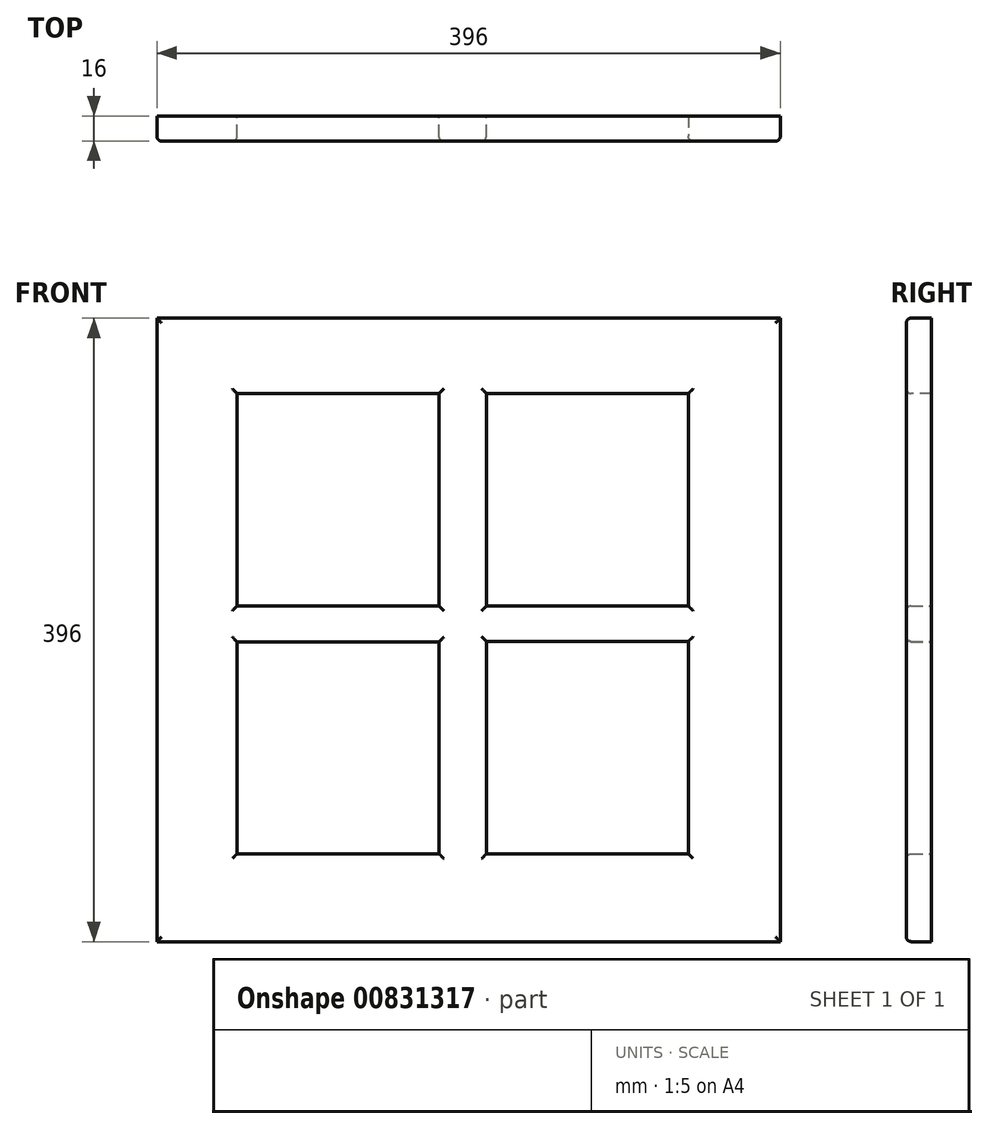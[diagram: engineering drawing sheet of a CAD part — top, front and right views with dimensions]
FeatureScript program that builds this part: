
annotation { "Feature Type Name" : "Feature", "Feature Type Description" : "" }
export const myFeature = defineFeature(function(context is Context, id is Id, definition is map)
    precondition{}
    {
        {
            var Q0;
            Q0=qCreatedBy(makeId("Front.planeOp"),FACE);
            var sketch = newSketch(context, id + "F0", { "sketchPlane" : qUnion([Q0])});
            skLineSegment(sketch, "E0.bottom", {"start": v(0, 0) * mm, "end": v(46.27, 0) * mm});
            skLineSegment(sketch, "E0.top", {"start": v(0, 37.42) * mm, "end": v(46.27, 37.42) * mm});
            skLineSegment(sketch, "E0.left", {"start": v(0, 0) * mm, "end": v(0, 37.42) * mm});
            skLineSegment(sketch, "E0.right", {"start": v(46.27, 0) * mm, "end": v(46.27, 37.42) * mm});
            skSolve(sketch);
        }
        {
            var Q0;
            Q0=makeQuery(id+"F0.imprint","IMPRINT",FACE,{"disambiguationData":[TD([[makeQuery(id+"F0.imprint","IMPRINT",EDGE,{"derivedFrom":sQuery(id+"F0.wireOp",EDGE,"E0.bottom")}),1.0]])]});
            extrude(context, id + "F1", {"entities" : qUnion([Q0]), "depth" : 16 * mm, "offsetDistance" : 25.4 * mm});
        }
        {
            var Q0;
            Q0=makeQuery(id+"F1.opExtrude","SWEPT_FACE",FACE,{"disambiguationData":[OSD([sQuery(id+"F0.wireOp",EDGE,"E0.left")])]});
            extrude(context, id + "F2", {"entities" : qUnion([Q0]), "operationType" : NewBodyOperationType.ADD, "oppositeDirection" : true, "depth" : 396 * mm, "offsetDistance" : 25 * mm});
        }
        {
            var Q0;
            {var subQ0=sQuery(id+"F0.wireOp",EDGE,"E0.bottom");Q0=makeQuery(id+"F2.boolean.opBoolean","MERGE",FACE,{"derivedFrom":[makeQuery(id+"F1.opExtrude","SWEPT_FACE",FACE,{"disambiguationData":[OSD([subQ0])]}),makeQuery(id+"F2.opExtrude","SWEPT_FACE",FACE,{"disambiguationData":[OSD([subQ0,sQuery(id+"F0.wireOp",EDGE,"E0.left")])]})]});}
            extrude(context, id + "F3", {"entities" : qUnion([Q0]), "operationType" : NewBodyOperationType.ADD, "oppositeDirection" : true, "depth" : 396 * mm, "offsetDistance" : 25 * mm});
        }
        {
            var Q0;
            {var subQ0=sQuery(id+"F0.wireOp",EDGE,"E0.left");var subQ1=sQuery(id+"F0.wireOp",EDGE,"E0.bottom");Q0=makeQuery(id+"F3.boolean.opBoolean","MERGE",FACE,{"derivedFrom":[makeQuery(id+"F2.boolean.opBoolean","MERGE",FACE,{"derivedFrom":[makeQuery(id+"F1.opExtrude","CAP_FACE",FACE,{"disambiguationData":[OSD([subQ1,sQuery(id+"F0.wireOp",EDGE,"E0.top"),subQ0,sQuery(id+"F0.wireOp",EDGE,"E0.right")])],"isStart":false}),makeQuery(id+"F2.opExtrude","SWEPT_FACE",FACE,{"disambiguationData":[OSD([subQ0]),TDD([makeQuery(id+"F1.opExtrude","CAP_EDGE",EDGE,{"disambiguationData":[OSD([subQ0])],"isStart":false})])]})]}),makeQuery(id+"F3.opExtrude","SWEPT_FACE",FACE,{"disambiguationData":[OSD([subQ1,subQ0]),TDD([makeQuery(id+"F2.boolean.opBoolean","MERGE",EDGE,{"derivedFrom":[makeQuery(id+"F1.opExtrude","CAP_EDGE",EDGE,{"disambiguationData":[OSD([subQ1])],"isStart":false}),makeQuery(id+"F2.opExtrude","SWEPT_EDGE",EDGE,{"disambiguationData":[OSD([subQ1,subQ0]),TDD([makeQuery(id+"F1.opExtrude","CAP_VERTEX",VERTEX,{"disambiguationData":[OSD([subQ1,subQ0])],"isStart":false})])]})]})])]})]});}
            var sketch = newSketch(context, id + "F4", { "sketchPlane" : qUnion([Q0])});
            skLineSegment(sketch, "E1.bottom", {"start": v(50.94, 348.18) * mm, "end": v(337.58, 348.18) * mm});
            skLineSegment(sketch, "E1.top", {"start": v(50.94, 55.76) * mm, "end": v(337.58, 55.76) * mm});
            skLineSegment(sketch, "E1.left", {"start": v(50.94, 348.18) * mm, "end": v(50.94, 55.76) * mm});
            skLineSegment(sketch, "E1.right", {"start": v(337.58, 348.18) * mm, "end": v(337.58, 55.76) * mm});
            skSolve(sketch);
        }
        {
            var Q0;
            Q0=makeQuery(id+"F4.imprint","IMPRINT",FACE,{"disambiguationData":[TD([[makeQuery(id+"F4.imprint","IMPRINT",EDGE,{"derivedFrom":sQuery(id+"F4.wireOp",EDGE,"E1.bottom")}),-1.0]])]});
            extrude(context, id + "F5", {"entities" : qUnion([Q0]), "operationType" : NewBodyOperationType.REMOVE, "oppositeDirection" : true, "depth" : 5 * mm, "offsetDistance" : 25 * mm});
        }
        {
            var Q0;
            Q0=makeQuery(id+"F5.boolean.opBoolean","COPY",FACE,{"derivedFrom":makeQuery(id+"F5.opExtrude","CAP_FACE",FACE,{"disambiguationData":[OSD([sQuery(id+"F4.wireOp",EDGE,"E1.bottom"),sQuery(id+"F4.wireOp",EDGE,"E1.top"),sQuery(id+"F4.wireOp",EDGE,"E1.left"),sQuery(id+"F4.wireOp",EDGE,"E1.right")])],"isStart":false})});
            var sketch = newSketch(context, id + "F6", { "sketchPlane" : qUnion([Q0])});
            skLineSegment(sketch, "E2.bottom", {"start": v(50.94, 348.18) * mm, "end": v(162.4, 348.18) * mm});
            skLineSegment(sketch, "E2.top", {"start": v(50.94, 257.7) * mm, "end": v(162.4, 257.7) * mm});
            skLineSegment(sketch, "E2.left", {"start": v(50.94, 348.18) * mm, "end": v(50.94, 257.7) * mm});
            skLineSegment(sketch, "E2.right", {"start": v(162.4, 348.18) * mm, "end": v(162.4, 257.7) * mm});
            skLineSegment(sketch, "E3.bottom", {"start": v(337.58, 348.18) * mm, "end": v(211.11, 348.18) * mm});
            skLineSegment(sketch, "E3.top", {"start": v(337.58, 256.78) * mm, "end": v(211.11, 256.78) * mm});
            skLineSegment(sketch, "E3.left", {"start": v(337.58, 348.18) * mm, "end": v(337.58, 256.78) * mm});
            skLineSegment(sketch, "E3.right", {"start": v(211.11, 348.18) * mm, "end": v(211.11, 256.78) * mm});
            skLineSegment(sketch, "E4.bottom", {"start": v(337.58, 55.76) * mm, "end": v(207.53, 55.76) * mm});
            skLineSegment(sketch, "E4.top", {"start": v(337.58, 219.35) * mm, "end": v(207.53, 219.35) * mm});
            skLineSegment(sketch, "E4.left", {"start": v(337.58, 55.76) * mm, "end": v(337.58, 219.35) * mm});
            skLineSegment(sketch, "E4.right", {"start": v(207.53, 55.76) * mm, "end": v(207.53, 219.35) * mm});
            skLineSegment(sketch, "E5.bottom", {"start": v(50.94, 55.76) * mm, "end": v(160.55, 55.76) * mm});
            skLineSegment(sketch, "E5.top", {"start": v(50.94, 215.04) * mm, "end": v(160.55, 215.04) * mm});
            skLineSegment(sketch, "E5.left", {"start": v(50.94, 55.76) * mm, "end": v(50.94, 215.04) * mm});
            skLineSegment(sketch, "E5.right", {"start": v(160.55, 55.76) * mm, "end": v(160.55, 215.04) * mm});
            skSolve(sketch);
        }
        {
            var Q0;
            {var subQ5=sQuery(id+"F6.wireOp",EDGE,"E2.top");Q0=makeQuery(id+"F6.imprint","IMPRINT",FACE,{"disambiguationData":[TD([[makeQuery(id+"F6.imprint","IMPRINT",EDGE,{"derivedFrom":subQ5}),-1.0]])]});}
            extrude(context, id + "F7", {"entities" : qUnion([Q0]), "operationType" : NewBodyOperationType.ADD, "depth" : 5 * mm, "offsetDistance" : 25 * mm});
        }
        {
            var Q0;
            Q0=makeQuery(id+"F7.opExtrude","SWEPT_FACE",FACE,{"disambiguationData":[OSD([sQuery(id+"F6.wireOp",EDGE,"E5.top")])]});
            extrude(context, id + "F8", {"entities" : qUnion([Q0]), "operationType" : NewBodyOperationType.ADD, "depth" : 24.58 * mm, "offsetDistance" : 25 * mm});
        }
        {
            var Q0;
            Q0=makeQuery(id+"F7.opExtrude","SWEPT_FACE",FACE,{"disambiguationData":[OSD([sQuery(id+"F6.wireOp",EDGE,"E4.top")])]});
            extrude(context, id + "F9", {"entities" : qUnion([Q0]), "operationType" : NewBodyOperationType.ADD, "depth" : 28.59 * mm, "offsetDistance" : 25 * mm});
        }
        {
            var Q0;
            Q0=makeQuery(id+"F7.opExtrude","SWEPT_FACE",FACE,{"disambiguationData":[OSD([sQuery(id+"F6.wireOp",EDGE,"E2.top")])]});
            extrude(context, id + "F10", {"entities" : qUnion([Q0]), "operationType" : NewBodyOperationType.REMOVE, "oppositeDirection" : true, "depth" : 44.5 * mm, "offsetDistance" : 25 * mm});
        }
        {
            var Q0;
            Q0=makeQuery(id+"F7.opExtrude","SWEPT_FACE",FACE,{"disambiguationData":[OSD([sQuery(id+"F6.wireOp",EDGE,"E3.top")])]});
            extrude(context, id + "F11", {"entities" : qUnion([Q0]), "operationType" : NewBodyOperationType.REMOVE, "oppositeDirection" : true, "depth" : 43.6 * mm, "offsetDistance" : 25 * mm});
        }
        {
            var Q0;
            {var subQ0=sQuery(id+"F6.wireOp",EDGE,"E2.right");Q0=makeQuery(id+"F10.boolean.opBoolean","MERGE",FACE,{"derivedFrom":[makeQuery(id+"F7.opExtrude","SWEPT_FACE",FACE,{"disambiguationData":[OSD([subQ0])]}),makeQuery(id+"F10.opExtrude","SWEPT_FACE",FACE,{"disambiguationData":[OSD([sQuery(id+"F6.wireOp",EDGE,"E2.top"),subQ0])]})]});}
            extrude(context, id + "F12", {"entities" : qUnion([Q0]), "operationType" : NewBodyOperationType.REMOVE, "oppositeDirection" : true, "depth" : 23.54 * mm, "offsetDistance" : 25 * mm});
        }
        {
            var Q0;
            Q0=makeQuery(id+"F7.opExtrude","SWEPT_FACE",FACE,{"disambiguationData":[OSD([sQuery(id+"F6.wireOp",EDGE,"E5.right")])]});
            extrude(context, id + "F13", {"entities" : qUnion([Q0]), "operationType" : NewBodyOperationType.REMOVE, "oppositeDirection" : true, "depth" : 25.4 * mm, "offsetDistance" : 25 * mm});
        }
        {
            var Q0;
            {var subQ0=sQuery(id+"F6.wireOp",EDGE,"E3.right");Q0=makeQuery(id+"F11.boolean.opBoolean","MERGE",FACE,{"derivedFrom":[makeQuery(id+"F7.opExtrude","SWEPT_FACE",FACE,{"disambiguationData":[OSD([subQ0])]}),makeQuery(id+"F11.opExtrude","SWEPT_FACE",FACE,{"disambiguationData":[OSD([sQuery(id+"F6.wireOp",EDGE,"E3.top"),subQ0])]})]});}
            extrude(context, id + "F14", {"entities" : qUnion([Q0]), "operationType" : NewBodyOperationType.REMOVE, "oppositeDirection" : true, "depth" : 8.54 * mm, "offsetDistance" : 25 * mm});
        }
        {
            var Q0;
            Q0=makeQuery(id+"F12.boolean.opBoolean","COPY",FACE,{"derivedFrom":makeQuery(id+"F12.opExtrude","CAP_FACE",FACE,{"disambiguationData":[OSD([sQuery(id+"F6.wireOp",EDGE,"E2.top"),sQuery(id+"F6.wireOp",EDGE,"E2.right")])],"isStart":false})});
            extrude(context, id + "F15", {"entities" : qUnion([Q0]), "operationType" : NewBodyOperationType.ADD, "depth" : 6.68 * mm, "offsetDistance" : 25 * mm});
        }
        {
            var Q0;
            Q0=makeQuery(id+"F14.boolean.opBoolean","COPY",FACE,{"derivedFrom":makeQuery(id+"F14.opExtrude","CAP_FACE",FACE,{"disambiguationData":[OSD([sQuery(id+"F6.wireOp",EDGE,"E3.top"),sQuery(id+"F6.wireOp",EDGE,"E3.right")])],"isStart":false})});
            extrude(context, id + "F16", {"entities" : qUnion([Q0]), "operationType" : NewBodyOperationType.ADD, "depth" : 6.68 * mm, "offsetDistance" : 25 * mm});
        }
        {
            var Q0;
            Q0=makeQuery(id+"F13.boolean.opBoolean","COPY",FACE,{"derivedFrom":makeQuery(id+"F13.opExtrude","CAP_FACE",FACE,{"disambiguationData":[OSD([sQuery(id+"F6.wireOp",EDGE,"E5.right")])],"isStart":false})});
            extrude(context, id + "F17", {"entities" : qUnion([Q0]), "operationType" : NewBodyOperationType.ADD, "depth" : 6.68 * mm, "offsetDistance" : 25 * mm});
        }
        {
            var Q0;
            Q0=makeQuery(id+"F7.opExtrude","SWEPT_FACE",FACE,{"disambiguationData":[OSD([sQuery(id+"F6.wireOp",EDGE,"E4.right")])]});
            extrude(context, id + "F18", {"entities" : qUnion([Q0]), "operationType" : NewBodyOperationType.ADD, "depth" : 1.72 * mm, "offsetDistance" : 25 * mm});
        }
        {
            var Q0;
            {var subQ0=sQuery(id+"F6.wireOp",EDGE,"E5.right");var subQ1=sQuery(id+"F4.wireOp",EDGE,"E1.top");var subQ2=sQuery(id+"F4.wireOp",EDGE,"E1.left");Q0=makeQuery(id+"F13.boolean.opBoolean","MERGE",FACE,{"derivedFrom":[makeQuery(id+"F7.boolean.opBoolean","SPLIT",FACE,{"disambiguationData":[TD([makeQuery(id+"F7.opExtrude","SWEPT_FACE",FACE,{"disambiguationData":[OSD([sQuery(id+"F6.wireOp",EDGE,"E5.top")])]})])],"derivedFrom":makeQuery(id+"F5.boolean.opBoolean","COPY",FACE,{"derivedFrom":makeQuery(id+"F5.opExtrude","CAP_FACE",FACE,{"disambiguationData":[OSD([sQuery(id+"F4.wireOp",EDGE,"E1.bottom"),subQ1,subQ2,sQuery(id+"F4.wireOp",EDGE,"E1.right")])],"isStart":false})})}),makeQuery(id+"F13.opExtrude","SWEPT_FACE",FACE,{"disambiguationData":[OSD([subQ0]),TDD([makeQuery(id+"F7.opExtrude","CAP_EDGE",EDGE,{"disambiguationData":[OSD([subQ0])],"isStart":true})])]})]});}
            var Q1;
            {var subQ0=sQuery(id+"F6.wireOp",EDGE,"E3.right");var subQ1=sQuery(id+"F6.wireOp",EDGE,"E3.top");var subQ2=sQuery(id+"F4.wireOp",EDGE,"E1.bottom");var subQ3=sQuery(id+"F4.wireOp",EDGE,"E1.right");Q1=makeQuery(id+"F14.boolean.opBoolean","MERGE",FACE,{"derivedFrom":[makeQuery(id+"F11.boolean.opBoolean","MERGE",FACE,{"derivedFrom":[makeQuery(id+"F7.boolean.opBoolean","SPLIT",FACE,{"disambiguationData":[TD([makeQuery(id+"F7.opExtrude","SWEPT_FACE",FACE,{"disambiguationData":[OSD([subQ1])]})])],"derivedFrom":makeQuery(id+"F5.boolean.opBoolean","COPY",FACE,{"derivedFrom":makeQuery(id+"F5.opExtrude","CAP_FACE",FACE,{"disambiguationData":[OSD([subQ2,sQuery(id+"F4.wireOp",EDGE,"E1.top"),sQuery(id+"F4.wireOp",EDGE,"E1.left"),subQ3])],"isStart":false})})}),makeQuery(id+"F11.opExtrude","SWEPT_FACE",FACE,{"disambiguationData":[OSD([subQ1]),TDD([makeQuery(id+"F7.opExtrude","CAP_EDGE",EDGE,{"disambiguationData":[OSD([subQ1])],"isStart":true})])]})]}),makeQuery(id+"F14.opExtrude","SWEPT_FACE",FACE,{"disambiguationData":[OSD([subQ1,subQ0]),TDD([makeQuery(id+"F11.boolean.opBoolean","MERGE",EDGE,{"derivedFrom":[makeQuery(id+"F7.opExtrude","CAP_EDGE",EDGE,{"disambiguationData":[OSD([subQ0])],"isStart":true}),makeQuery(id+"F11.opExtrude","SWEPT_EDGE",EDGE,{"disambiguationData":[OSD([subQ1,subQ0]),TDD([makeQuery(id+"F7.opExtrude","CAP_VERTEX",VERTEX,{"disambiguationData":[OSD([subQ1,subQ0])],"isStart":true})])]})]})])]})]});}
            var Q2;
            {var subQ0=sQuery(id+"F4.wireOp",EDGE,"E1.top");var subQ1=sQuery(id+"F4.wireOp",EDGE,"E1.right");Q2=makeQuery(id+"F7.boolean.opBoolean","SPLIT",FACE,{"disambiguationData":[TD([makeQuery(id+"F7.opExtrude","SWEPT_FACE",FACE,{"disambiguationData":[OSD([sQuery(id+"F6.wireOp",EDGE,"E4.top")])]})])],"derivedFrom":makeQuery(id+"F5.boolean.opBoolean","COPY",FACE,{"derivedFrom":makeQuery(id+"F5.opExtrude","CAP_FACE",FACE,{"disambiguationData":[OSD([sQuery(id+"F4.wireOp",EDGE,"E1.bottom"),subQ0,sQuery(id+"F4.wireOp",EDGE,"E1.left"),subQ1])],"isStart":false})})});}
            var Q3;
            {var subQ0=sQuery(id+"F6.wireOp",EDGE,"E2.right");var subQ1=sQuery(id+"F6.wireOp",EDGE,"E2.top");var subQ2=sQuery(id+"F4.wireOp",EDGE,"E1.bottom");var subQ3=sQuery(id+"F4.wireOp",EDGE,"E1.left");Q3=makeQuery(id+"F12.boolean.opBoolean","MERGE",FACE,{"derivedFrom":[makeQuery(id+"F10.boolean.opBoolean","MERGE",FACE,{"derivedFrom":[makeQuery(id+"F7.boolean.opBoolean","SPLIT",FACE,{"disambiguationData":[TD([makeQuery(id+"F7.opExtrude","SWEPT_FACE",FACE,{"disambiguationData":[OSD([subQ1])]})])],"derivedFrom":makeQuery(id+"F5.boolean.opBoolean","COPY",FACE,{"derivedFrom":makeQuery(id+"F5.opExtrude","CAP_FACE",FACE,{"disambiguationData":[OSD([subQ2,sQuery(id+"F4.wireOp",EDGE,"E1.top"),subQ3,sQuery(id+"F4.wireOp",EDGE,"E1.right")])],"isStart":false})})}),makeQuery(id+"F10.opExtrude","SWEPT_FACE",FACE,{"disambiguationData":[OSD([subQ1]),TDD([makeQuery(id+"F7.opExtrude","CAP_EDGE",EDGE,{"disambiguationData":[OSD([subQ1])],"isStart":true})])]})]}),makeQuery(id+"F12.opExtrude","SWEPT_FACE",FACE,{"disambiguationData":[OSD([subQ1,subQ0]),TDD([makeQuery(id+"F10.boolean.opBoolean","MERGE",EDGE,{"derivedFrom":[makeQuery(id+"F7.opExtrude","CAP_EDGE",EDGE,{"disambiguationData":[OSD([subQ0])],"isStart":true}),makeQuery(id+"F10.opExtrude","SWEPT_EDGE",EDGE,{"disambiguationData":[OSD([subQ1,subQ0]),TDD([makeQuery(id+"F7.opExtrude","CAP_VERTEX",VERTEX,{"disambiguationData":[OSD([subQ1,subQ0])],"isStart":true})])]})]})])]})]});}
            extrude(context, id + "F19", {"entities" : qUnion([Q0, Q1, Q2, Q3]), "operationType" : NewBodyOperationType.REMOVE, "oppositeDirection" : true, "depth" : 11 * mm, "offsetDistance" : 25 * mm});
        }
        {
            var Q0;
            {var subQ0=sQuery(id+"F6.wireOp",EDGE,"E4.right");var subQ1=sQuery(id+"F6.wireOp",EDGE,"E5.right");var subQ2=sQuery(id+"F6.wireOp",EDGE,"E3.right");var subQ3=sQuery(id+"F6.wireOp",EDGE,"E3.top");var subQ4=sQuery(id+"F6.wireOp",EDGE,"E2.right");var subQ5=sQuery(id+"F6.wireOp",EDGE,"E2.top");var subQ6=sQuery(id+"F6.wireOp",EDGE,"E4.top");var subQ7=sQuery(id+"F6.wireOp",EDGE,"E5.top");var subQ8=sQuery(id+"F0.wireOp",EDGE,"E0.left");var subQ9=sQuery(id+"F0.wireOp",EDGE,"E0.bottom");Q0=makeQuery(id+"F18.boolean.opBoolean","MERGE",FACE,{"derivedFrom":[makeQuery(id+"F17.boolean.opBoolean","MERGE",FACE,{"derivedFrom":[makeQuery(id+"F16.boolean.opBoolean","MERGE",FACE,{"derivedFrom":[makeQuery(id+"F15.boolean.opBoolean","MERGE",FACE,{"derivedFrom":[makeQuery(id+"F9.boolean.opBoolean","MERGE",FACE,{"derivedFrom":[makeQuery(id+"F8.boolean.opBoolean","MERGE",FACE,{"derivedFrom":[makeQuery(id+"F7.boolean.opBoolean","MERGE",FACE,{"derivedFrom":[makeQuery(id+"F3.boolean.opBoolean","MERGE",FACE,{"derivedFrom":[makeQuery(id+"F2.boolean.opBoolean","MERGE",FACE,{"derivedFrom":[makeQuery(id+"F1.opExtrude","CAP_FACE",FACE,{"disambiguationData":[OSD([subQ9,sQuery(id+"F0.wireOp",EDGE,"E0.top"),subQ8,sQuery(id+"F0.wireOp",EDGE,"E0.right")])],"isStart":false}),makeQuery(id+"F2.opExtrude","SWEPT_FACE",FACE,{"disambiguationData":[OSD([subQ8]),TDD([makeQuery(id+"F1.opExtrude","CAP_EDGE",EDGE,{"disambiguationData":[OSD([subQ8])],"isStart":false})])]})]}),makeQuery(id+"F3.opExtrude","SWEPT_FACE",FACE,{"disambiguationData":[OSD([subQ9,subQ8]),TDD([makeQuery(id+"F2.boolean.opBoolean","MERGE",EDGE,{"derivedFrom":[makeQuery(id+"F1.opExtrude","CAP_EDGE",EDGE,{"disambiguationData":[OSD([subQ9])],"isStart":false}),makeQuery(id+"F2.opExtrude","SWEPT_EDGE",EDGE,{"disambiguationData":[OSD([subQ9,subQ8]),TDD([makeQuery(id+"F1.opExtrude","CAP_VERTEX",VERTEX,{"disambiguationData":[OSD([subQ9,subQ8])],"isStart":false})])]})]})])]})]}),makeQuery(id+"F7.opExtrude","CAP_FACE",FACE,{"disambiguationData":[OSD([sQuery(id+"F4.wireOp",EDGE,"E1.bottom"),sQuery(id+"F4.wireOp",EDGE,"E1.top"),sQuery(id+"F4.wireOp",EDGE,"E1.left"),sQuery(id+"F4.wireOp",EDGE,"E1.right"),subQ5,subQ4,subQ3,subQ2,subQ6,subQ0,subQ7,subQ1])],"isStart":false})]}),makeQuery(id+"F8.opExtrude","SWEPT_FACE",FACE,{"disambiguationData":[OSD([subQ7]),TDD([makeQuery(id+"F7.opExtrude","CAP_EDGE",EDGE,{"disambiguationData":[OSD([subQ7])],"isStart":false})])]})]}),makeQuery(id+"F9.opExtrude","SWEPT_FACE",FACE,{"disambiguationData":[OSD([subQ6]),TDD([makeQuery(id+"F7.opExtrude","CAP_EDGE",EDGE,{"disambiguationData":[OSD([subQ6])],"isStart":false})])]})]}),makeQuery(id+"F15.opExtrude","SWEPT_FACE",FACE,{"disambiguationData":[OSD([subQ5,subQ4]),TDD([makeQuery(id+"F12.boolean.opBoolean","COPY",EDGE,{"derivedFrom":makeQuery(id+"F12.opExtrude","CAP_EDGE",EDGE,{"disambiguationData":[OSD([subQ5,subQ4]),TDD([makeQuery(id+"F10.boolean.opBoolean","MERGE",EDGE,{"derivedFrom":[makeQuery(id+"F7.opExtrude","CAP_EDGE",EDGE,{"disambiguationData":[OSD([subQ4])],"isStart":false}),makeQuery(id+"F10.opExtrude","SWEPT_EDGE",EDGE,{"disambiguationData":[OSD([subQ5,subQ4]),TDD([makeQuery(id+"F7.opExtrude","CAP_VERTEX",VERTEX,{"disambiguationData":[OSD([subQ5,subQ4])],"isStart":false})])]})]})])],"isStart":false})})])]})]}),makeQuery(id+"F16.opExtrude","SWEPT_FACE",FACE,{"disambiguationData":[OSD([subQ3,subQ2]),TDD([makeQuery(id+"F14.boolean.opBoolean","COPY",EDGE,{"derivedFrom":makeQuery(id+"F14.opExtrude","CAP_EDGE",EDGE,{"disambiguationData":[OSD([subQ3,subQ2]),TDD([makeQuery(id+"F11.boolean.opBoolean","MERGE",EDGE,{"derivedFrom":[makeQuery(id+"F7.opExtrude","CAP_EDGE",EDGE,{"disambiguationData":[OSD([subQ2])],"isStart":false}),makeQuery(id+"F11.opExtrude","SWEPT_EDGE",EDGE,{"disambiguationData":[OSD([subQ3,subQ2]),TDD([makeQuery(id+"F7.opExtrude","CAP_VERTEX",VERTEX,{"disambiguationData":[OSD([subQ3,subQ2])],"isStart":false})])]})]})])],"isStart":false})})])]})]}),makeQuery(id+"F17.opExtrude","SWEPT_FACE",FACE,{"disambiguationData":[OSD([subQ1]),TDD([makeQuery(id+"F13.boolean.opBoolean","COPY",EDGE,{"derivedFrom":makeQuery(id+"F13.opExtrude","CAP_EDGE",EDGE,{"disambiguationData":[OSD([subQ1]),TDD([makeQuery(id+"F7.opExtrude","CAP_EDGE",EDGE,{"disambiguationData":[OSD([subQ1])],"isStart":false})])],"isStart":false})})])]})]}),makeQuery(id+"F18.opExtrude","SWEPT_FACE",FACE,{"disambiguationData":[OSD([subQ0]),TDD([makeQuery(id+"F7.opExtrude","CAP_EDGE",EDGE,{"disambiguationData":[OSD([subQ0])],"isStart":false})])]})]});}
            fillet(context, id + "F20", {"entities" : qUnion([Q0]), "radius" : 3 * mm, "tangentPropagation" : true, "allowEdgeOverflow" : false});
        }
    });
